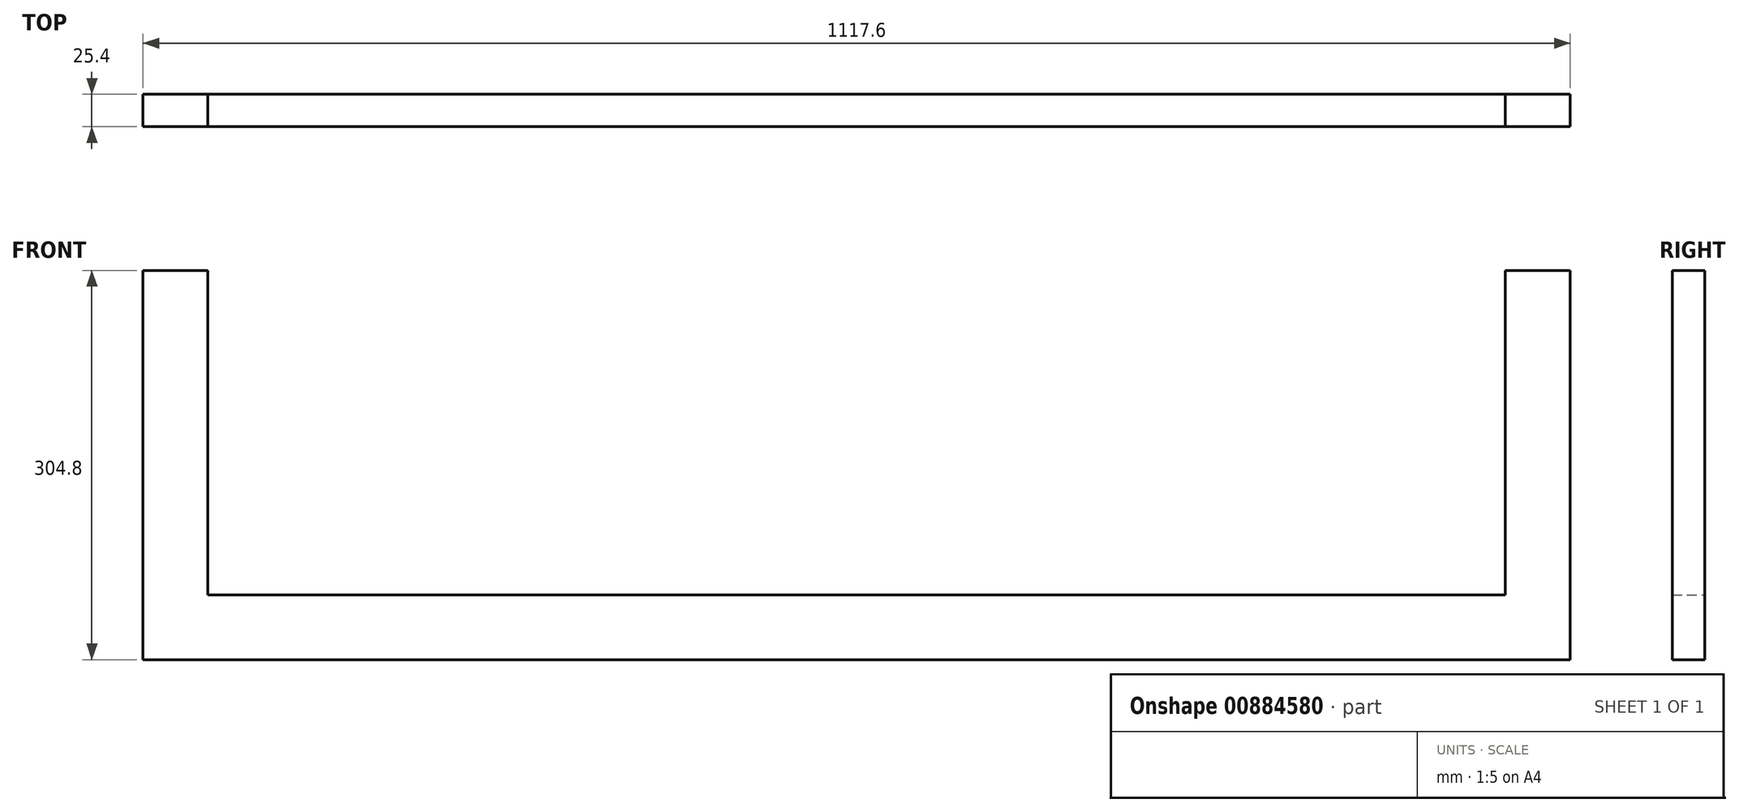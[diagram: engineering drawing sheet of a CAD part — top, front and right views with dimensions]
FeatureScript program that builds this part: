
annotation { "Feature Type Name" : "Feature", "Feature Type Description" : "" }
export const myFeature = defineFeature(function(context is Context, id is Id, definition is map)
    precondition{}
    {
        {
            var Q0;
            Q0=qCreatedBy(makeId("Front.planeOp"),FACE);
            var sketch = newSketch(context, id + "F0", { "sketchPlane" : qUnion([Q0])});
            skLineSegment(sketch, "E0", {"start": v(-486.12, 0) * mm, "end": v(631.48, 0) * mm});
            skLineSegment(sketch, "E1", {"start": v(631.48, 0) * mm, "end": v(631.48, 304.8) * mm});
            skLineSegment(sketch, "E2", {"start": v(631.48, 304.8) * mm, "end": v(580.68, 304.8) * mm});
            skLineSegment(sketch, "E3", {"start": v(580.68, 304.8) * mm, "end": v(580.68, 50.8) * mm});
            skLineSegment(sketch, "E4", {"start": v(580.68, 50.8) * mm, "end": v(-435.32, 50.8) * mm});
            skLineSegment(sketch, "E5", {"start": v(-435.32, 50.8) * mm, "end": v(-435.32, 304.8) * mm});
            skLineSegment(sketch, "E6", {"start": v(-435.32, 304.8) * mm, "end": v(-486.12, 304.8) * mm});
            skLineSegment(sketch, "E7", {"start": v(-486.12, 304.8) * mm, "end": v(-486.12, 0) * mm});
            skSolve(sketch);
        }
        {
            var Q0;
            Q0 = qSketchRegion(id + "F0", true);
            extrude(context, id + "F1", {"entities" : qUnion([Q0]), "depth" : 25.4 * mm, "offsetDistance" : 25.4 * mm});
        }
    });
